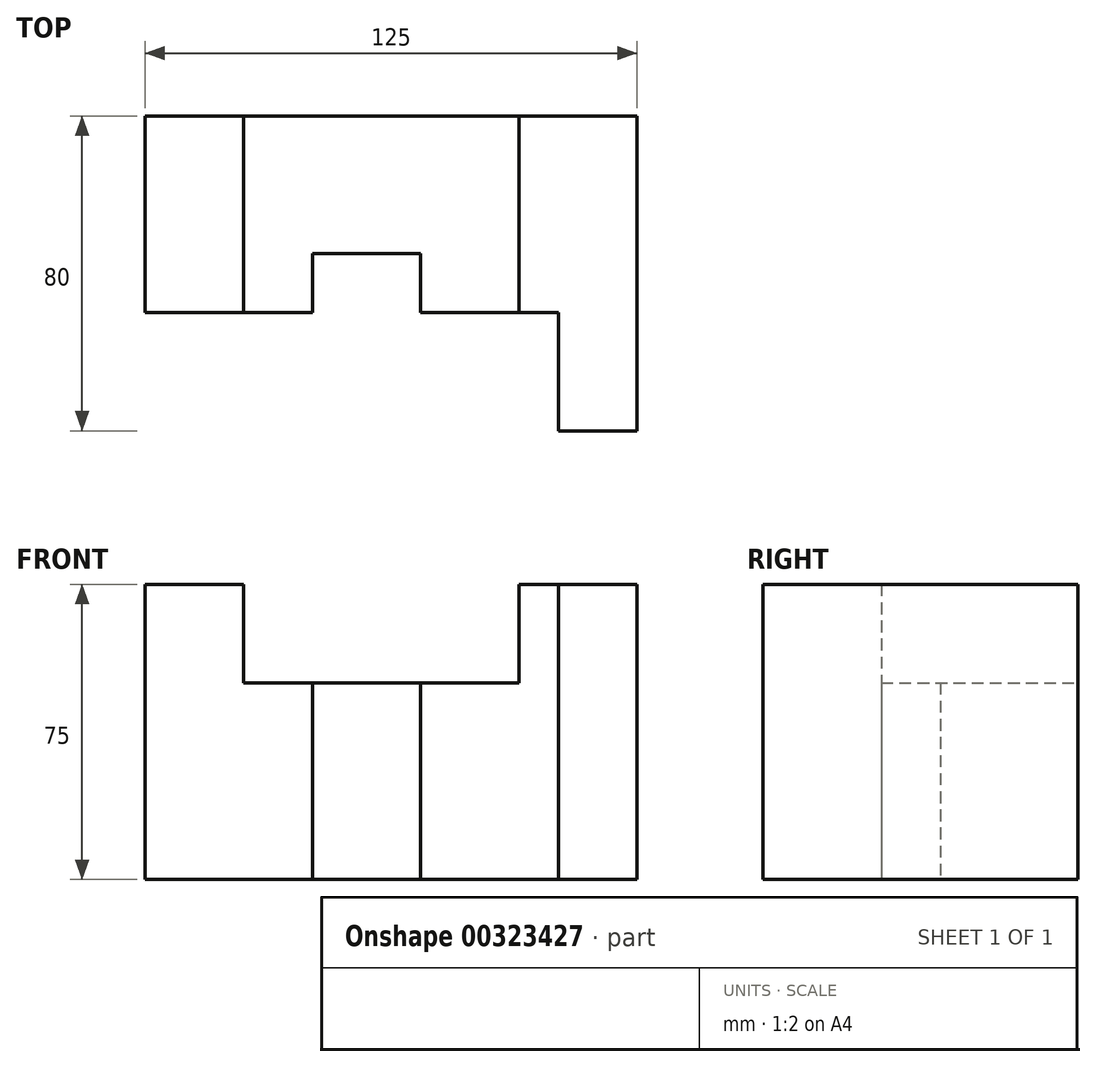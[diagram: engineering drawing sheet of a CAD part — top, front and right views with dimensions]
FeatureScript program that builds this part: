
annotation { "Feature Type Name" : "Feature", "Feature Type Description" : "" }
export const myFeature = defineFeature(function(context is Context, id is Id, definition is map)
    precondition{}
    {
        {
            var Q0;
            Q0=qCreatedBy(makeId("Front.planeOp"),FACE);
            var sketch = newSketch(context, id + "F0", { "sketchPlane" : qUnion([Q0])});
            skLineSegment(sketch, "E0.bottom", {"start": v(0, 0) * mm, "end": v(25, 0) * mm});
            skLineSegment(sketch, "E0.top", {"start": v(0, 75) * mm, "end": v(25, 75) * mm});
            skLineSegment(sketch, "E0.left", {"start": v(0, 0) * mm, "end": v(0, 75) * mm});
            skLineSegment(sketch, "E0.right", {"start": v(25, 0) * mm, "end": v(25, 75) * mm});
            skLineSegment(sketch, "E1.bottom", {"start": v(25, 50) * mm, "end": v(42.5, 50) * mm});
            skLineSegment(sketch, "E1.top", {"start": v(25, 0) * mm, "end": v(42.5, 0) * mm});
            skLineSegment(sketch, "E1.left", {"start": v(25, 50) * mm, "end": v(25, 0) * mm});
            skLineSegment(sketch, "E1.right", {"start": v(42.5, 50) * mm, "end": v(42.5, 0) * mm});
            skSolve(sketch);
        }
        {
            var Q0;
            Q0 = qSketchRegion(id + "F0", true);
            extrude(context, id + "F1", {"entities" : qUnion([Q0]), "depth" : 50 * mm});
        }
        {
            var Q0;
            Q0=makeQuery(id+"F1.opExtrude","SWEPT_FACE",FACE,{"disambiguationData":[OSD([sQuery(id+"F0.wireOp",EDGE,"E1.right")])]});
            var sketch = newSketch(context, id + "F2", { "sketchPlane" : qUnion([Q0])});
            skLineSegment(sketch, "E2.bottom", {"start": v(0, 50) * mm, "end": v(-35, 50) * mm});
            skLineSegment(sketch, "E2.top", {"start": v(0, 0) * mm, "end": v(-35, 0) * mm});
            skLineSegment(sketch, "E2.left", {"start": v(0, 50) * mm, "end": v(0, 0) * mm});
            skLineSegment(sketch, "E2.right", {"start": v(-35, 50) * mm, "end": v(-35, 0) * mm});
            skSolve(sketch);
        }
        {
            var Q0;
            Q0=makeQuery(id+"F2.imprint","IMPRINT",FACE,{"disambiguationData":[TD([[makeQuery(id+"F2.imprint","IMPRINT",EDGE,{"derivedFrom":sQuery(id+"F2.wireOp",EDGE,"E2.bottom")}),-1.0]])]});
            extrude(context, id + "F3", {"entities" : qUnion([Q0]), "operationType" : NewBodyOperationType.ADD, "depth" : 27.5 * mm});
        }
        {
            var Q0;
            Q0=makeQuery(id+"F3.opExtrude","CAP_FACE",FACE,{"disambiguationData":[OSD([sQuery(id+"F2.wireOp",EDGE,"E2.bottom"),sQuery(id+"F2.wireOp",EDGE,"E2.top"),sQuery(id+"F2.wireOp",EDGE,"E2.left"),sQuery(id+"F2.wireOp",EDGE,"E2.right")])],"isStart":false});
            var sketch = newSketch(context, id + "F4", { "sketchPlane" : qUnion([Q0])});
            skLineSegment(sketch, "E3.bottom", {"start": v(0, 50) * mm, "end": v(-50, 50) * mm});
            skLineSegment(sketch, "E3.top", {"start": v(0, 0) * mm, "end": v(-50, 0) * mm});
            skLineSegment(sketch, "E3.left", {"start": v(0, 50) * mm, "end": v(0, 0) * mm});
            skLineSegment(sketch, "E3.right", {"start": v(-50, 50) * mm, "end": v(-50, 0) * mm});
            skSolve(sketch);
        }
        {
            var Q0;
            Q0 = qSketchRegion(id + "F4", true);
            extrude(context, id + "F5", {"entities" : qUnion([Q0]), "operationType" : NewBodyOperationType.ADD, "depth" : 25 * mm});
        }
        {
            var Q0;
            Q0=makeQuery(id+"F5.opExtrude","CAP_FACE",FACE,{"disambiguationData":[OSD([sQuery(id+"F4.wireOp",EDGE,"E3.bottom"),sQuery(id+"F4.wireOp",EDGE,"E3.top"),sQuery(id+"F4.wireOp",EDGE,"E3.left"),sQuery(id+"F4.wireOp",EDGE,"E3.right")])],"isStart":false});
            var sketch = newSketch(context, id + "F6", { "sketchPlane" : qUnion([Q0])});
            skLineSegment(sketch, "E4.bottom", {"start": v(0, 0) * mm, "end": v(-50, 0) * mm});
            skLineSegment(sketch, "E4.top", {"start": v(0, 75) * mm, "end": v(-50, 75) * mm});
            skLineSegment(sketch, "E4.left", {"start": v(0, 0) * mm, "end": v(0, 75) * mm});
            skLineSegment(sketch, "E4.right", {"start": v(-50, 0) * mm, "end": v(-50, 75) * mm});
            skSolve(sketch);
        }
        {
            var Q0;
            Q0 = qSketchRegion(id + "F6", true);
            extrude(context, id + "F7", {"entities" : qUnion([Q0]), "operationType" : NewBodyOperationType.ADD, "depth" : 30 * mm});
        }
        {
            var Q0;
            Q0=makeQuery(id+"F7.boolean.opBoolean","MERGE",FACE,{"derivedFrom":[makeQuery(id+"F5.opExtrude","SWEPT_FACE",FACE,{"disambiguationData":[OSD([sQuery(id+"F4.wireOp",EDGE,"E3.right")])]}),makeQuery(id+"F7.opExtrude","SWEPT_FACE",FACE,{"disambiguationData":[OSD([sQuery(id+"F6.wireOp",EDGE,"E4.right")])]})]});
            var sketch = newSketch(context, id + "F8", { "sketchPlane" : qUnion([Q0])});
            skLineSegment(sketch, "E5.bottom", {"start": v(125, 75) * mm, "end": v(105, 75) * mm});
            skLineSegment(sketch, "E5.top", {"start": v(125, 0) * mm, "end": v(105, 0) * mm});
            skLineSegment(sketch, "E5.left", {"start": v(125, 75) * mm, "end": v(125, 0) * mm});
            skLineSegment(sketch, "E5.right", {"start": v(105, 75) * mm, "end": v(105, 0) * mm});
            skSolve(sketch);
        }
        {
            var Q0;
            Q0 = qSketchRegion(id + "F8", true);
            extrude(context, id + "F9", {"entities" : qUnion([Q0]), "operationType" : NewBodyOperationType.ADD, "depth" : 30 * mm});
        }
    });
